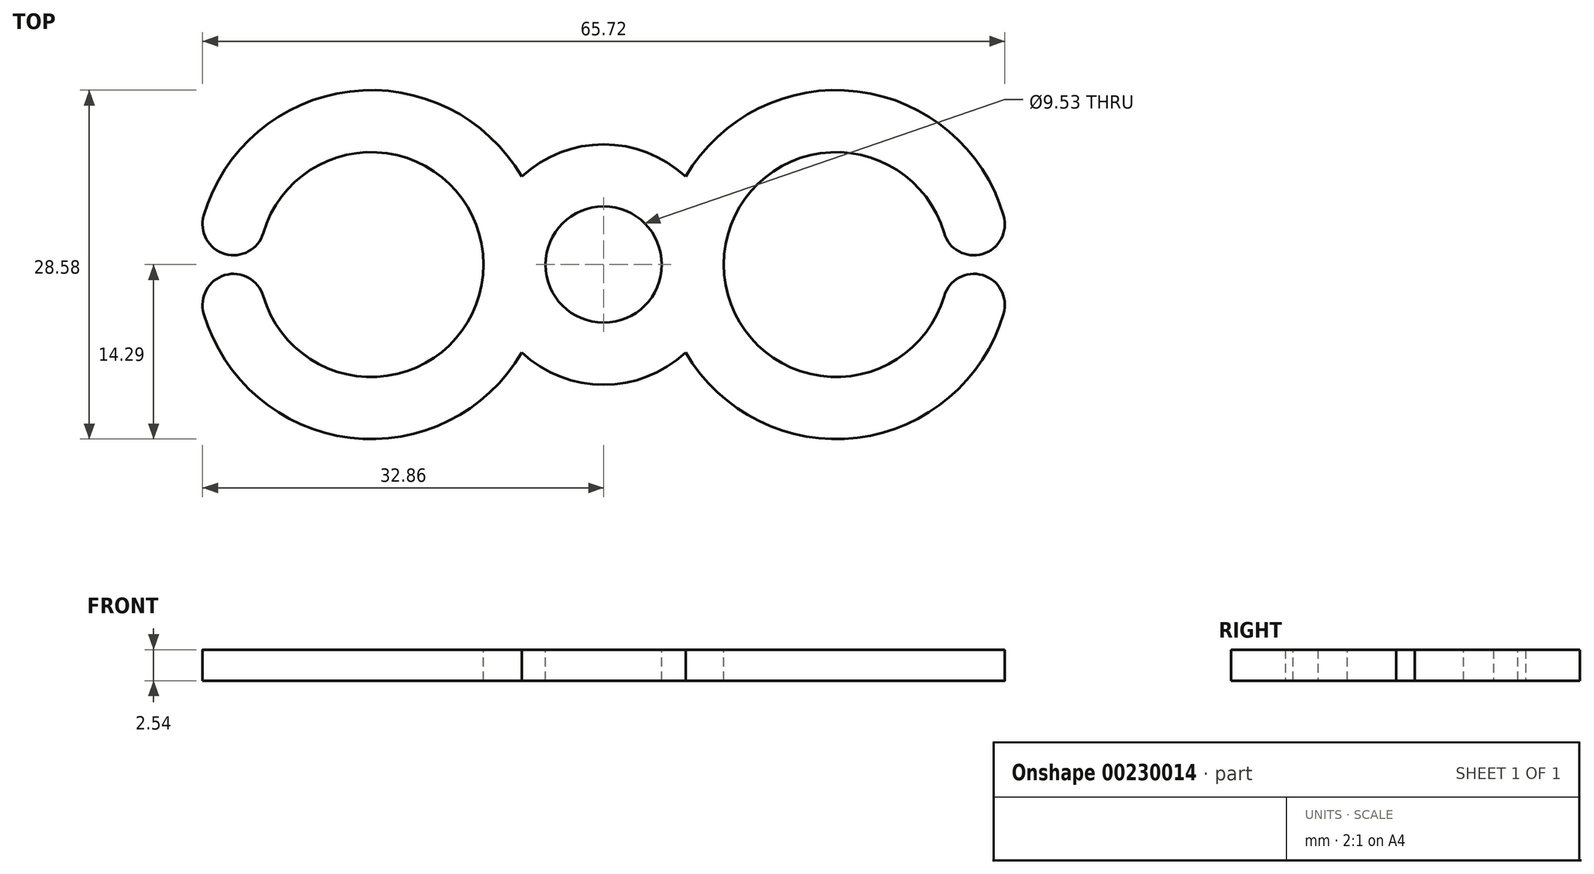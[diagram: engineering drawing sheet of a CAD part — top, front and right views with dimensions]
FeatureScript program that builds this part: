
annotation { "Feature Type Name" : "Feature", "Feature Type Description" : "" }
export const myFeature = defineFeature(function(context is Context, id is Id, definition is map)
    precondition{}
    {
        {
            var Q0;
            Q0=qCreatedBy(makeId("Top.planeOp"),FACE);
            var sketch = newSketch(context, id + "F0", { "sketchPlane" : qUnion([Q0])});
            skCircle(sketch, "E0", {"center": v(-19.05, 0) * mm, "radius": 14.29 * mm});
            skCircle(sketch, "E1", {"center": v(19.05, 0) * mm, "radius": 14.29 * mm});
            skLineSegment(sketch, "E2", {"start": v(-19.05, 0) * mm, "end": v(19.05, 0) * mm, "construction": true});
            skCircle(sketch, "E3", {"center": v(0, 0) * mm, "radius": 9.84 * mm});
            skLineSegment(sketch, "E4", {"start": v(-19.05, 14.29) * mm, "end": v(19.05, 14.29) * mm, "construction": true});
            skLineSegment(sketch, "E5", {"start": v(19.05, -14.29) * mm, "end": v(-19.05, -14.29) * mm, "construction": true});
            skPoint(sketch, "E6", {"position": v(-9.84, 0) * mm});
            skPoint(sketch, "E7", {"position": v(-4.76, 0) * mm});
            skSolve(sketch);
        }
        {
            var Q0;
            Q0 = qSketchRegion(id + "F0", true);
            extrude(context, id + "F1", {"entities" : qUnion([Q0]), "endBound" : BoundingType.SYMMETRIC, "depth" : 2.54 * mm});
        }
        {
            var Q0;
            Q0=makeQuery(id+"F1.opExtrude","CAP_FACE",FACE,{"disambiguationData":[OSD([sQuery(id+"F0.wireOp",EDGE,"E0"),sQuery(id+"F0.wireOp",EDGE,"E1"),sQuery(id+"F0.wireOp",EDGE,"E3")])],"isStart":false});
            var sketch = newSketch(context, id + "F2", { "sketchPlane" : qUnion([Q0])});
            skCircle(sketch, "E8", {"center": v(-19.05, 0) * mm, "radius": 9.2 * mm});
            skCircle(sketch, "E9", {"center": v(19.05, 0) * mm, "radius": 9.2 * mm});
            skCircle(sketch, "E10", {"center": v(0, 0) * mm, "radius": 4.76 * mm});
            skSolve(sketch);
        }
        {
            var Q0;
            Q0 = qSketchRegion(id + "F2", true);
            extrude(context, id + "F3", {"entities" : qUnion([Q0]), "operationType" : NewBodyOperationType.REMOVE, "oppositeDirection" : true, "depth" : 25.4 * mm});
        }
        {
            var Q0;
            Q0=makeQuery(id+"F1.opExtrude","CAP_FACE",FACE,{"disambiguationData":[OSD([sQuery(id+"F0.wireOp",EDGE,"E0"),sQuery(id+"F0.wireOp",EDGE,"E1"),sQuery(id+"F0.wireOp",EDGE,"E3")])],"isStart":false});
            var sketch = newSketch(context, id + "F4", { "sketchPlane" : qUnion([Q0])});
            skLineSegment(sketch, "E11", {"start": v(-19.05, 0) * mm, "end": v(-33.34, 0) * mm, "construction": true});
            skLineSegment(sketch, "E12.bottom", {"start": v(-33.34, 0.76) * mm, "end": v(-16.58, 0.76) * mm});
            skLineSegment(sketch, "E12.top", {"start": v(-33.34, -0.76) * mm, "end": v(-16.58, -0.76) * mm});
            skLineSegment(sketch, "E12.left", {"start": v(-33.34, 0.76) * mm, "end": v(-33.34, -0.76) * mm});
            skLineSegment(sketch, "E12.right", {"start": v(-16.58, 0.76) * mm, "end": v(-16.58, -0.76) * mm});
            skLineSegment(sketch, "E13", {"start": v(0, -0.63) * mm, "end": v(0, 19.69) * mm, "construction": true});
            skLineSegment(sketch, "E14.MirrorCS", {"start": v(16.58, 0.76) * mm, "end": v(16.58, -0.76) * mm});
            skLineSegment(sketch, "E15.MirrorCS", {"start": v(33.34, 0.76) * mm, "end": v(33.34, -0.76) * mm});
            skLineSegment(sketch, "E16.MirrorCS", {"start": v(19.05, 0) * mm, "end": v(33.34, 0) * mm, "construction": true});
            skLineSegment(sketch, "E17.MirrorCS", {"start": v(33.34, 0.76) * mm, "end": v(16.58, 0.76) * mm});
            skLineSegment(sketch, "E18.MirrorCS", {"start": v(33.34, -0.76) * mm, "end": v(16.58, -0.76) * mm});
            skSolve(sketch);
        }
        {
            var Q0;
            Q0 = qSketchRegion(id + "F4", true);
            extrude(context, id + "F5", {"entities" : qUnion([Q0]), "operationType" : NewBodyOperationType.REMOVE, "oppositeDirection" : true, "depth" : 25.4 * mm});
        }
        {
            var Q0;
            Q0=makeQuery(id+"F5.boolean.opBoolean","INTERSECT",EDGE,{"derivedFrom":[makeQuery(id+"F1.opExtrude","SWEPT_FACE",FACE,{"disambiguationData":[OSD([sQuery(id+"F0.wireOp",EDGE,"E0")])]}),makeQuery(id+"F5.opExtrude","SWEPT_FACE",FACE,{"disambiguationData":[OSD([sQuery(id+"F4.wireOp",EDGE,"E12.bottom")])]})]});
            var Q1;
            Q1=makeQuery(id+"F5.boolean.opBoolean","INTERSECT",EDGE,{"derivedFrom":[makeQuery(id+"F3.boolean.opBoolean","COPY",FACE,{"derivedFrom":makeQuery(id+"F3.opExtrude","SWEPT_FACE",FACE,{"disambiguationData":[OSD([sQuery(id+"F2.wireOp",EDGE,"E8")])]})}),makeQuery(id+"F5.opExtrude","SWEPT_FACE",FACE,{"disambiguationData":[OSD([sQuery(id+"F4.wireOp",EDGE,"E12.bottom")])]})]});
            var Q2;
            Q2=makeQuery(id+"F5.boolean.opBoolean","INTERSECT",EDGE,{"derivedFrom":[makeQuery(id+"F3.boolean.opBoolean","COPY",FACE,{"derivedFrom":makeQuery(id+"F3.opExtrude","SWEPT_FACE",FACE,{"disambiguationData":[OSD([sQuery(id+"F2.wireOp",EDGE,"E8")])]})}),makeQuery(id+"F5.opExtrude","SWEPT_FACE",FACE,{"disambiguationData":[OSD([sQuery(id+"F4.wireOp",EDGE,"E12.top")])]})]});
            var Q3;
            Q3=makeQuery(id+"F5.boolean.opBoolean","INTERSECT",EDGE,{"derivedFrom":[makeQuery(id+"F1.opExtrude","SWEPT_FACE",FACE,{"disambiguationData":[OSD([sQuery(id+"F0.wireOp",EDGE,"E0")])]}),makeQuery(id+"F5.opExtrude","SWEPT_FACE",FACE,{"disambiguationData":[OSD([sQuery(id+"F4.wireOp",EDGE,"E12.top")])]})]});
            var Q4;
            Q4=makeQuery(id+"F5.boolean.opBoolean","INTERSECT",EDGE,{"derivedFrom":[makeQuery(id+"F3.boolean.opBoolean","COPY",FACE,{"derivedFrom":makeQuery(id+"F3.opExtrude","SWEPT_FACE",FACE,{"disambiguationData":[OSD([sQuery(id+"F2.wireOp",EDGE,"E9")])]})}),makeQuery(id+"F5.opExtrude","SWEPT_FACE",FACE,{"disambiguationData":[OSD([sQuery(id+"F4.wireOp",EDGE,"E18.MirrorCS")])]})]});
            var Q5;
            Q5=makeQuery(id+"F5.boolean.opBoolean","INTERSECT",EDGE,{"derivedFrom":[makeQuery(id+"F3.boolean.opBoolean","COPY",FACE,{"derivedFrom":makeQuery(id+"F3.opExtrude","SWEPT_FACE",FACE,{"disambiguationData":[OSD([sQuery(id+"F2.wireOp",EDGE,"E9")])]})}),makeQuery(id+"F5.opExtrude","SWEPT_FACE",FACE,{"disambiguationData":[OSD([sQuery(id+"F4.wireOp",EDGE,"E17.MirrorCS")])]})]});
            var Q6;
            Q6=makeQuery(id+"F5.boolean.opBoolean","INTERSECT",EDGE,{"derivedFrom":[makeQuery(id+"F1.opExtrude","SWEPT_FACE",FACE,{"disambiguationData":[OSD([sQuery(id+"F0.wireOp",EDGE,"E1")])]}),makeQuery(id+"F5.opExtrude","SWEPT_FACE",FACE,{"disambiguationData":[OSD([sQuery(id+"F4.wireOp",EDGE,"E17.MirrorCS")])]})]});
            var Q7;
            Q7=makeQuery(id+"F5.boolean.opBoolean","INTERSECT",EDGE,{"derivedFrom":[makeQuery(id+"F1.opExtrude","SWEPT_FACE",FACE,{"disambiguationData":[OSD([sQuery(id+"F0.wireOp",EDGE,"E1")])]}),makeQuery(id+"F5.opExtrude","SWEPT_FACE",FACE,{"disambiguationData":[OSD([sQuery(id+"F4.wireOp",EDGE,"E18.MirrorCS")])]})]});
            fillet(context, id + "F6", {"entities" : qUnion([Q0, Q1, Q2, Q3, Q4, Q5, Q6, Q7]), "radius" : 2.54 * mm, "tangentPropagation" : true, "allowEdgeOverflow" : false});
        }
    });
